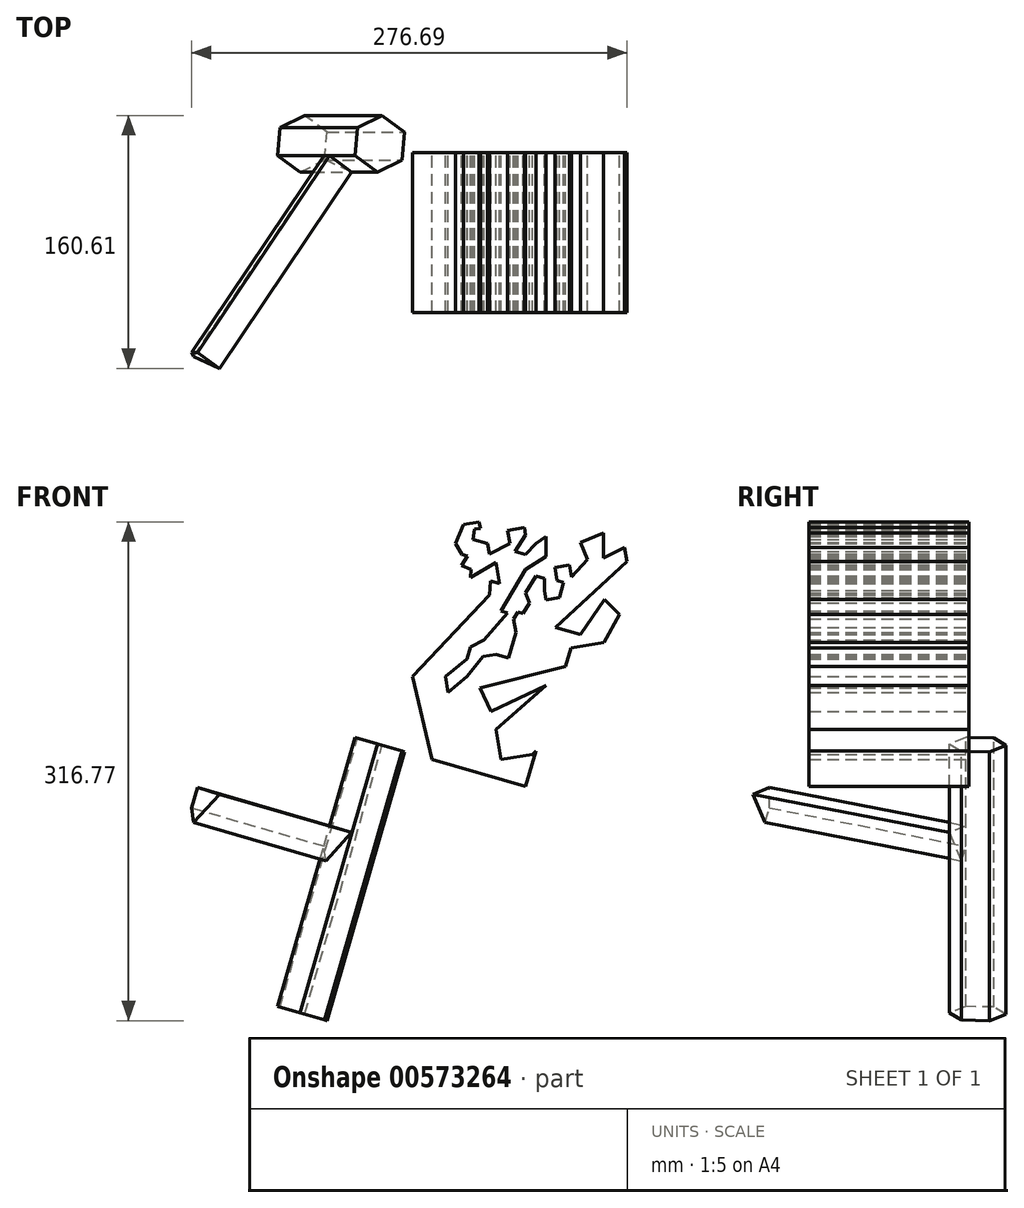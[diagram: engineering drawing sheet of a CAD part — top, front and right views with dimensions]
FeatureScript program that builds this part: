
annotation { "Feature Type Name" : "Feature", "Feature Type Description" : "" }
export const myFeature = defineFeature(function(context is Context, id is Id, definition is map)
    precondition{}
    {
        {
            var Q0;
            Q0=qCreatedBy(makeId("Front.planeOp"),FACE);
            var sketch = newSketch(context, id + "F0", { "sketchPlane" : qUnion([Q0])});
            skLineSegment(sketch, "E0", {"start": v(-68.84, 62.2) * mm, "end": v(-117.68, 10.46) * mm});
            skLineSegment(sketch, "E1", {"start": v(-117.68, 10.46) * mm, "end": v(-105.13, -42.56) * mm});
            skLineSegment(sketch, "E2", {"start": v(-105.13, -42.56) * mm, "end": v(-45.78, -59.68) * mm});
            skLineSegment(sketch, "E3", {"start": v(-45.78, -59.68) * mm, "end": v(-39.24, -37) * mm});
            skLineSegment(sketch, "E4", {"start": v(-41.37, -39.07) * mm, "end": v(-61.38, -42.56) * mm});
            skLineSegment(sketch, "E5", {"start": v(-61.38, -42.56) * mm, "end": v(-64.7, -23.5) * mm});
            skLineSegment(sketch, "E6", {"start": v(-41.37, -39.07) * mm, "end": v(-39.24, -37) * mm});
            skLineSegment(sketch, "E7", {"start": v(-64.7, -23.5) * mm, "end": v(-32.9, 4.75) * mm});
            skLineSegment(sketch, "E8", {"start": v(-32.9, 4.75) * mm, "end": v(-67.83, -11.78) * mm});
            skLineSegment(sketch, "E9", {"start": v(-67.83, -11.78) * mm, "end": v(-74.8, 2.95) * mm});
            skLineSegment(sketch, "E10", {"start": v(-74.8, 2.95) * mm, "end": v(-20.35, 16.5) * mm});
            skLineSegment(sketch, "E11", {"start": v(-20.35, 16.5) * mm, "end": v(-16.9, 28.43) * mm});
            skLineSegment(sketch, "E12", {"start": v(-16.9, 28.43) * mm, "end": v(3.83, 32.04) * mm});
            skLineSegment(sketch, "E13", {"start": v(3.83, 32.04) * mm, "end": v(13.9, 49.8) * mm});
            skLineSegment(sketch, "E14", {"start": v(13.9, 49.8) * mm, "end": v(4.4, 59.26) * mm});
            skLineSegment(sketch, "E15", {"start": v(4.4, 59.26) * mm, "end": v(-10.85, 36.88) * mm});
            skLineSegment(sketch, "E16", {"start": v(-10.85, 36.88) * mm, "end": v(-26.7, 41.46) * mm});
            skLineSegment(sketch, "E17", {"start": v(-26.7, 41.46) * mm, "end": v(18.65, 83.38) * mm});
            skLineSegment(sketch, "E18", {"start": v(18.65, 83.38) * mm, "end": v(17.1, 92.26) * mm});
            skLineSegment(sketch, "E19", {"start": v(17.1, 92.26) * mm, "end": v(3.73, 85.52) * mm});
            skLineSegment(sketch, "E20", {"start": v(3.73, 85.52) * mm, "end": v(3.73, 101.46) * mm});
            skLineSegment(sketch, "E21", {"start": v(3.73, 101.46) * mm, "end": v(-10.85, 95.55) * mm});
            skLineSegment(sketch, "E22", {"start": v(-10.85, 95.55) * mm, "end": v(-6.44, 84.66) * mm});
            skLineSegment(sketch, "E23", {"start": v(-6.44, 84.66) * mm, "end": v(-16.62, 73.54) * mm});
            skLineSegment(sketch, "E24", {"start": v(-16.62, 73.54) * mm, "end": v(-17.93, 81.1) * mm});
            skLineSegment(sketch, "E25", {"start": v(-17.93, 81.1) * mm, "end": v(-27.27, 79.48) * mm});
            skLineSegment(sketch, "E26", {"start": v(-27.27, 79.48) * mm, "end": v(-25.86, 71.33) * mm});
            skLineSegment(sketch, "E27", {"start": v(-25.86, 71.33) * mm, "end": v(-21.62, 70.1) * mm});
            skLineSegment(sketch, "E28", {"start": v(-21.62, 70.1) * mm, "end": v(-24.4, 60.47) * mm});
            skLineSegment(sketch, "E29", {"start": v(-24.4, 60.47) * mm, "end": v(-32.9, 59) * mm});
            skLineSegment(sketch, "E30", {"start": v(-32.9, 59) * mm, "end": v(-33.92, 64.9) * mm});
            skLineSegment(sketch, "E31", {"start": v(-33.92, 64.9) * mm, "end": v(-33.92, 72.67) * mm});
            skLineSegment(sketch, "E32", {"start": v(-33.92, 72.67) * mm, "end": v(-39.24, 74.2) * mm});
            skLineSegment(sketch, "E33", {"start": v(-39.24, 74.2) * mm, "end": v(-45.78, 63.43) * mm});
            skLineSegment(sketch, "E34", {"start": v(-45.78, 63.43) * mm, "end": v(-43.4, 57) * mm});
            skLineSegment(sketch, "E35", {"start": v(-43.4, 57) * mm, "end": v(-47.48, 50.39) * mm});
            skLineSegment(sketch, "E36", {"start": v(-47.48, 50.39) * mm, "end": v(-50.7, 51.32) * mm});
            skLineSegment(sketch, "E37", {"start": v(-50.7, 51.32) * mm, "end": v(-53.58, 46.93) * mm});
            skLineSegment(sketch, "E38", {"start": v(-53.58, 46.93) * mm, "end": v(-52.09, 38.35) * mm});
            skLineSegment(sketch, "E39", {"start": v(-52.09, 38.35) * mm, "end": v(-56.8, 22.02) * mm});
            skLineSegment(sketch, "E40", {"start": v(-56.8, 22.02) * mm, "end": v(-64.7, 24.3) * mm});
            skLineSegment(sketch, "E41", {"start": v(-64.7, 24.3) * mm, "end": v(-72.94, 22.86) * mm});
            skLineSegment(sketch, "E42", {"start": v(-72.94, 22.86) * mm, "end": v(-83.09, 10.46) * mm});
            skLineSegment(sketch, "E43", {"start": v(-83.09, 10.46) * mm, "end": v(-94.96, 0) * mm});
            skLineSegment(sketch, "E44", {"start": v(-94.96, 0) * mm, "end": v(-96.78, 10.46) * mm});
            skLineSegment(sketch, "E45", {"start": v(-96.78, 10.46) * mm, "end": v(-83.09, 21.46) * mm});
            skLineSegment(sketch, "E46", {"start": v(-83.09, 21.46) * mm, "end": v(-80.93, 28.95) * mm});
            skLineSegment(sketch, "E47", {"start": v(-80.93, 28.95) * mm, "end": v(-72.23, 33.4) * mm});
            skLineSegment(sketch, "E48", {"start": v(-72.23, 33.4) * mm, "end": v(-57.31, 50.6) * mm});
            skLineSegment(sketch, "E49", {"start": v(-57.31, 50.6) * mm, "end": v(-61.38, 51.78) * mm});
            skLineSegment(sketch, "E50", {"start": v(-61.38, 51.78) * mm, "end": v(-45.78, 78.24) * mm});
            skLineSegment(sketch, "E51", {"start": v(-45.78, 78.24) * mm, "end": v(-32.9, 86.63) * mm});
            skLineSegment(sketch, "E52", {"start": v(-32.9, 86.63) * mm, "end": v(-32.9, 99.18) * mm});
            skLineSegment(sketch, "E53", {"start": v(-32.9, 99.18) * mm, "end": v(-39.24, 94.74) * mm});
            skLineSegment(sketch, "E54", {"start": v(-39.24, 94.74) * mm, "end": v(-45.78, 87.84) * mm});
            skLineSegment(sketch, "E55", {"start": v(-45.78, 87.84) * mm, "end": v(-52.66, 89.83) * mm});
            skLineSegment(sketch, "E56", {"start": v(-52.66, 89.83) * mm, "end": v(-45.78, 100.2) * mm});
            skLineSegment(sketch, "E57", {"start": v(-45.78, 100.2) * mm, "end": v(-46.6, 104.88) * mm});
            skLineSegment(sketch, "E58", {"start": v(-46.6, 104.88) * mm, "end": v(-57.23, 103.03) * mm});
            skLineSegment(sketch, "E59", {"start": v(-57.23, 103.03) * mm, "end": v(-55.79, 94.74) * mm});
            skLineSegment(sketch, "E60", {"start": v(-55.79, 94.74) * mm, "end": v(-68.84, 87.97) * mm});
            skLineSegment(sketch, "E61", {"start": v(-68.84, 87.97) * mm, "end": v(-70.02, 94.74) * mm});
            skLineSegment(sketch, "E62", {"start": v(-70.02, 94.74) * mm, "end": v(-72.9, 95.57) * mm});
            skLineSegment(sketch, "E63", {"start": v(-72.9, 95.57) * mm, "end": v(-79.37, 97.44) * mm});
            skLineSegment(sketch, "E64", {"start": v(-79.37, 97.44) * mm, "end": v(-78.34, 103.88) * mm});
            skLineSegment(sketch, "E65", {"start": v(-78.34, 103.88) * mm, "end": v(-74.6, 104.28) * mm});
            skLineSegment(sketch, "E66", {"start": v(-74.6, 104.28) * mm, "end": v(-75.33, 108.44) * mm});
            skLineSegment(sketch, "E67", {"start": v(-75.33, 108.44) * mm, "end": v(-85.42, 106.69) * mm});
            skLineSegment(sketch, "E68", {"start": v(-85.42, 106.69) * mm, "end": v(-90.2, 94.74) * mm});
            skLineSegment(sketch, "E69", {"start": v(-90.2, 94.74) * mm, "end": v(-86.14, 87.72) * mm});
            skLineSegment(sketch, "E70", {"start": v(-86.14, 87.72) * mm, "end": v(-82.75, 86.67) * mm});
            skLineSegment(sketch, "E71", {"start": v(-82.75, 86.67) * mm, "end": v(-86.48, 80.84) * mm});
            skLineSegment(sketch, "E72", {"start": v(-86.48, 80.84) * mm, "end": v(-80.37, 78.24) * mm});
            skLineSegment(sketch, "E73", {"start": v(-80.37, 78.24) * mm, "end": v(-80.71, 73.01) * mm});
            skLineSegment(sketch, "E74", {"start": v(-80.71, 73.01) * mm, "end": v(-64.7, 82.6) * mm});
            skLineSegment(sketch, "E75", {"start": v(-64.7, 82.6) * mm, "end": v(-62.4, 69.34) * mm});
            skLineSegment(sketch, "E76", {"start": v(-62.4, 69.34) * mm, "end": v(-68.05, 70.97) * mm});
            skLineSegment(sketch, "E77", {"start": v(-68.05, 70.97) * mm, "end": v(-68.84, 62.2) * mm});
            skSolve(sketch);
        }
        {
            var Q0;
            Q0=makeQuery(id+"F0.imprint","IMPRINT",FACE,{"disambiguationData":[TD([[makeQuery(id+"F0.imprint","IMPRINT",EDGE,{"derivedFrom":sQuery(id+"F0.wireOp",EDGE,"E0")}),1.0]])]});
            extrude(context, id + "F1", {"entities" : qUnion([Q0]), "depth" : 101.6 * mm, "offsetDistance" : 25.4 * mm});
        }
        {
            var Q0;
            Q0=makeQuery(id+"F1.opExtrude","SWEPT_FACE",FACE,{"disambiguationData":[OSD([sQuery(id+"F0.wireOp",EDGE,"E2")])]});
            var sketch = newSketch(context, id + "F2", { "sketchPlane" : qUnion([Q0])});
            skCircle(sketch, "E78.cCircle", {"center": v(-123.83, -5.46) * mm, "radius": 15.6 * mm, "construction": true});
            skLineSegment(sketch, "E78.0", {"start": v(-140.17, 2.15) * mm, "end": v(-125.41, 12.5) * mm});
            skLineSegment(sketch, "E78.1", {"start": v(-125.41, 12.5) * mm, "end": v(-109.07, 4.88) * mm});
            skLineSegment(sketch, "E78.2", {"start": v(-109.07, 4.88) * mm, "end": v(-107.5, -13.07) * mm});
            skLineSegment(sketch, "E78.3", {"start": v(-107.5, -13.07) * mm, "end": v(-122.25, -23.42) * mm});
            skLineSegment(sketch, "E78.4", {"start": v(-122.25, -23.42) * mm, "end": v(-138.59, -15.8) * mm});
            skLineSegment(sketch, "E78.5", {"start": v(-138.59, -15.8) * mm, "end": v(-140.17, 2.15) * mm});
            skPoint(sketch, "E78.0.midPoint", {"position": v(-132.8, 7.32) * mm});
            skSolve(sketch);
        }
        {
            var Q0;
            Q0=makeQuery(id+"F2.imprint","IMPRINT",FACE,{"disambiguationData":[TD([[makeQuery(id+"F2.imprint","IMPRINT",EDGE,{"derivedFrom":sQuery(id+"F2.wireOp",EDGE,"E78.0")}),-1.0]])]});
            extrude(context, id + "F3", {"entities" : qUnion([Q0]), "depth" : 177.8 * mm, "offsetDistance" : 25.4 * mm});
        }
        {
            var Q0;
            Q0=makeQuery(id+"F3.opExtrude","SWEPT_FACE",FACE,{"disambiguationData":[OSD([sQuery(id+"F2.wireOp",EDGE,"E78.0")])]});
            var sketch = newSketch(context, id + "F4", { "sketchPlane" : qUnion([Q0])});
            skCircle(sketch, "E79.cCircle", {"center": v(-147.46, -92) * mm, "radius": 7.33 * mm, "construction": true});
            skLineSegment(sketch, "E79.0", {"start": v(-133, -89.6) * mm, "end": v(-152.6, -105.74) * mm});
            skLineSegment(sketch, "E79.1", {"start": v(-152.6, -105.74) * mm, "end": v(-156.79, -80.7) * mm});
            skLineSegment(sketch, "E79.2", {"start": v(-156.79, -80.7) * mm, "end": v(-133, -89.6) * mm});
            skPoint(sketch, "E79.0.midPoint", {"position": v(-142.8, -97.66) * mm});
            skSolve(sketch);
        }
        {
            var Q0;
            {var subQ0=sQuery(id+"F4.wireOp",EDGE,"E79.0");Q0=makeQuery(id+"F4.imprint","IMPRINT",FACE,{"disambiguationData":[TD([[makeQuery(id+"F4.imprint","IMPRINT",EDGE,{"derivedFrom":subQ0}),-1.0]])]});}
            extrude(context, id + "F5", {"entities" : qUnion([Q0]), "operationType" : NewBodyOperationType.ADD, "depth" : 152.4 * mm, "offsetDistance" : 25.4 * mm});
        }
    });
